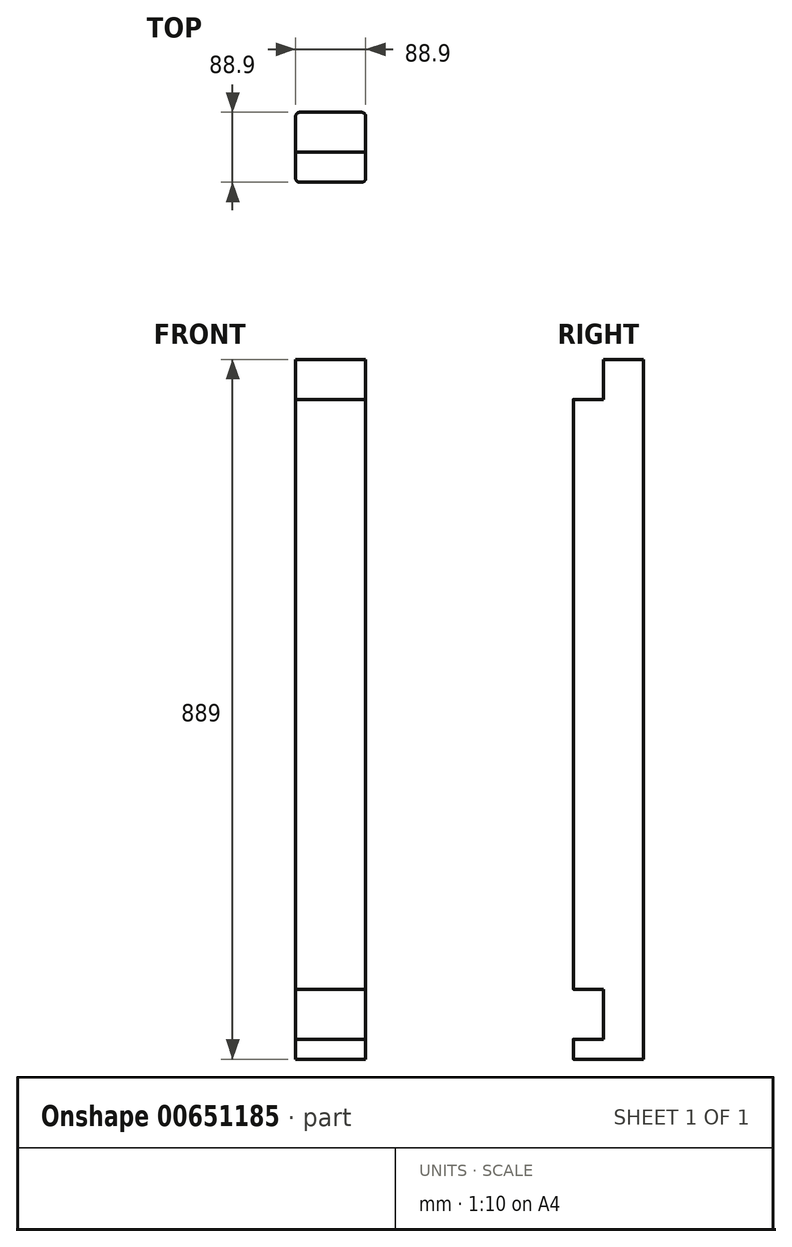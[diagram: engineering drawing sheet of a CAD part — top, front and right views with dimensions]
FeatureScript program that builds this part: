
annotation { "Feature Type Name" : "Feature", "Feature Type Description" : "" }
export const myFeature = defineFeature(function(context is Context, id is Id, definition is map)
    precondition{}
    {
        {
            var Q0;
            Q0=qCreatedBy(makeId("Right.planeOp"),FACE);
            var sketch = newSketch(context, id + "F0", { "sketchPlane" : qUnion([Q0])});
            skLineSegment(sketch, "E0", {"start": v(26.36, 525) * mm, "end": v(26.36, -364) * mm});
            skLineSegment(sketch, "E1", {"start": v(26.36, -364) * mm, "end": v(-62.54, -364) * mm});
            skLineSegment(sketch, "E2", {"start": v(-62.54, -364) * mm, "end": v(-62.54, -338.6) * mm});
            skLineSegment(sketch, "E3", {"start": v(-62.54, -338.6) * mm, "end": v(-24.44, -338.6) * mm});
            skLineSegment(sketch, "E4", {"start": v(-24.44, -338.6) * mm, "end": v(-24.44, -275.1) * mm});
            skLineSegment(sketch, "E5", {"start": v(-24.44, -275.1) * mm, "end": v(-62.54, -275.1) * mm});
            skLineSegment(sketch, "E6", {"start": v(-62.54, -275.1) * mm, "end": v(-62.54, 474.2) * mm});
            skLineSegment(sketch, "E7", {"start": v(-62.54, 474.2) * mm, "end": v(-24.44, 474.2) * mm});
            skLineSegment(sketch, "E8", {"start": v(-24.44, 474.2) * mm, "end": v(-24.44, 525) * mm});
            skLineSegment(sketch, "E9", {"start": v(-24.44, 525) * mm, "end": v(26.36, 525) * mm});
            skSolve(sketch);
        }
        {
            var Q0;
            Q0=makeQuery(id+"F0.imprint","IMPRINT",FACE,{"disambiguationData":[TD([[makeQuery(id+"F0.imprint","IMPRINT",EDGE,{"derivedFrom":sQuery(id+"F0.wireOp",EDGE,"E0")}),-1.0]])]});
            extrude(context, id + "F1", {"entities" : qUnion([Q0]), "depth" : 88.9 * mm, "offsetDistance" : 25.4 * mm, "symmetric" : true});
        }
        {
            var Q0;
            Q0=makeQuery(id+"F1.opExtrude","CAP_EDGE",EDGE,{"disambiguationData":[OSD([sQuery(id+"F0.wireOp",EDGE,"E6")])],"isStart":false});
            var Q1;
            Q1=makeQuery(id+"F1.opExtrude","CAP_EDGE",EDGE,{"disambiguationData":[OSD([sQuery(id+"F0.wireOp",EDGE,"E2")])],"isStart":false});
            var Q2;
            Q2=makeQuery(id+"F1.opExtrude","CAP_EDGE",EDGE,{"disambiguationData":[OSD([sQuery(id+"F0.wireOp",EDGE,"E2")])],"isStart":true});
            var Q3;
            Q3=makeQuery(id+"F1.opExtrude","CAP_EDGE",EDGE,{"disambiguationData":[OSD([sQuery(id+"F0.wireOp",EDGE,"E6")])],"isStart":true});
            var Q4;
            Q4=makeQuery(id+"F1.opExtrude","CAP_EDGE",EDGE,{"disambiguationData":[OSD([sQuery(id+"F0.wireOp",EDGE,"E0")])],"isStart":false});
            var Q5;
            Q5=makeQuery(id+"F1.opExtrude","CAP_EDGE",EDGE,{"disambiguationData":[OSD([sQuery(id+"F0.wireOp",EDGE,"E0")])],"isStart":true});
            fillet(context, id + "F2", {"entities" : qUnion([Q0, Q1, Q2, Q3, Q4, Q5]), "radius" : 5.08 * mm, "tangentPropagation" : true, "allowEdgeOverflow" : false});
        }
    });
